# Revit family: PRD_FrankeWS_PrssrRlfVlvs_AQUALINEWCFlushingValve_AQRM551_AQRM559
name_source: partatom
category: Plumbing Fixtures
revit_build: Autodesk Revit 2018 (Build: 20190510_1515(x64)
units: mm (PartAtom-declared; Revit-internal decimal feet)

## family parameters
Cut with Voids When Loaded = Yes
Host = Face
OmniClass Number = 23.45.05.14.17
OmniClass Title = Showers
Part Type = Normal
Room Calculation Point = No
Round Connector Dimension = Use Diameter
Shared = Yes

## types (2) — shared parameters
AssetType = Fixed
Category = Pr_65_54_95_65, Pressure relief valves
Default Elevation = 2000 mm  [stored 6.56168 ft]
DurationUnit = year
Features = for surface installation
FunctionalPrinciple = Hydraulic self-closing
HasIntegralShutOffDevice = Yes
IfcExportAs = IfcValveType
IfcExportType = FLUSHING
IsHighPressure = No
Manufacturer = KWC Group AG
ManufacturerName = KWC Group AG
ManufacturerURL = www.kwc.com
Material = Brass
MaximumFlowPressure = 4.00 bar
MaximumFlushWaterVolume = 9.00 liter
MinimumFlowPressure = 1.20 bar
MinimumFlushWaterVolume = 6.00 liter
NBSDescription = Pressure relief valves
NBSReference = 90-10-90/415
ProductInformation = https://pim.kwc.com
ProtectiveShutdown = No
ShowerMaterial = PRD_AR_ChromatedBrass_HighPolished
SoundInsulation = No
TypeOfFlushingFitting = WC flush valve
TypeOfMounting = Wall mounting
TypeOfOperation = Manual operation
URL = www.kwc.com
Uniclass2015Code = Pr_65_54_95_65
Uniclass2015Title = Pressure relief valves
Uniclass2015Version = Products v1.23
Version = 1
WarrantyDurationUnit = year
zero-valued in all types: NominalDepth, NominalHeight, NominalWidth

## per-type parameters (varying)
| type | AQRM551 | AQRM559 | BIMObjectName | BottomOffset | CalculationFlowRateColdWater | Description | DiameterNominal | Finish | Flow | FlushingRate | GrossWeight | InletSize | MaximumFlushingFlow | MinimumFlushingFlow | ModelNumber | Name | NetWeight | Offset | ProductCode |
| AQRM559 | No | Yes | PRD_AR_PressureReliefValves_AQUALINEWCFlushingValve_AQRM559 | 14 mm  [stored 0.0459318 ft] | 1.00 liter per second | AQUALINE WC flush valve for surface installation, flushing quantity and flow rate adjustable, all-metal construction. | 20  [stored 0.0656168 ft] | Chromed | 1.0 L/s | 1.0 L/s | 1.20 kg | DN 20 | 1.30 liter per second | 1.00 liter per second | 2000066508 | AQUALINE WC flushing valve AQRM559 | 1.02 kg | 146 mm  [stored 0.479003 ft] | 209.0000.019 |
| AQRM551 | Yes | No | PRD_AR_PressureReliefValves_AQUALINEWCFlushingValve_AQRM551 | 0 mm  [stored 0 ft] | 0.70 liter per second | AQUALINE WC flush valve for surface installation, flushing quantity and volume flow adjustable. With nominal diameter DN 15. Polished chromium-plated brass, push cap and screw fitting made of chromium-plated plastic. | 15  [stored 0.0492126 ft] | Polished chrome | 0.7 L/s | 0.7 L/s | 0.69 kg | DN 15 | 1.00 liter per second | 0.70 liter per second | 2000100082 | AQUALINE WC flushing valve AQRM551 | 0.61 kg | 104 mm | 209.0638.138 |

note: column(s) folded — value = type name in every type: Model, ModelReference

note: [stored X ft] marks values corroborated as IEEE doubles in the binary element streams (Revit-internal decimal feet)

## geometry (parser evidence)
native form markers: Sweep x2
no freeform markers — native parametric forms only
